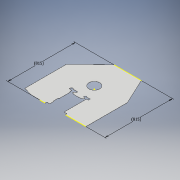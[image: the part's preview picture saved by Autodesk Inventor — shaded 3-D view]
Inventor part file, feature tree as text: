
AUTODESK INVENTOR PART (.ipt)
format: ipt  version: 2018 (Build 220112000, 112)  size: 230,400 bytes
history: native  units: mm
features: other x10, reference x8, sketch x4, extrude x3, plane x1
ambient origin geometry x8: Origin, YZ Plane, XZ Plane, XY Plane, X Axis, Y Axis, Z Axis, Center Point
bodies: Solid1 (feature_tree)
feature tree (26):
  other  "Table"
  other  "Cover V3-01"
  other  "Cover V3-02"
  plane  "Work Plane1"
  extrude  "Extrusion1"  Depth=500.0mm
  extrude  "Extrusion2"  Depth=530.0mm
  extrude  "Bed"  Depth=1.6mm
  sketch  "Sketch4"  dims[d22=1.6mm d23=0.0mm d25=300.0mm d26=1.6mm d27=0.0mm d28=2.0mm d29=1.6mm d30=0.0mm d31=815.0mm d32=815.0mm]
  sketch  "Sketch1"  dims[d9=815.0mm d10=500.0mm]
  reference  "Reference1"
  reference  "Reference2"
  reference  "Reference3"
  reference  "Reference4"
  reference  "Reference5"
  reference  "Reference6"
  reference  "Reference7"
  sketch  "Sketch2"  dims[d12=330.0mm d14=530.0mm]
  sketch  "Sketch3"  dims[d16=20.071286mm d17=1.6mm]
  reference  "Reference8"
  other  "Lathe Model 2018.iam"
  other  "front:1"
  other  "barrel:1"
  other  "X axis screw support:1"
  other  "chuck holder:1"
  other  "BED:1"
  other  "Gearbox:1"
